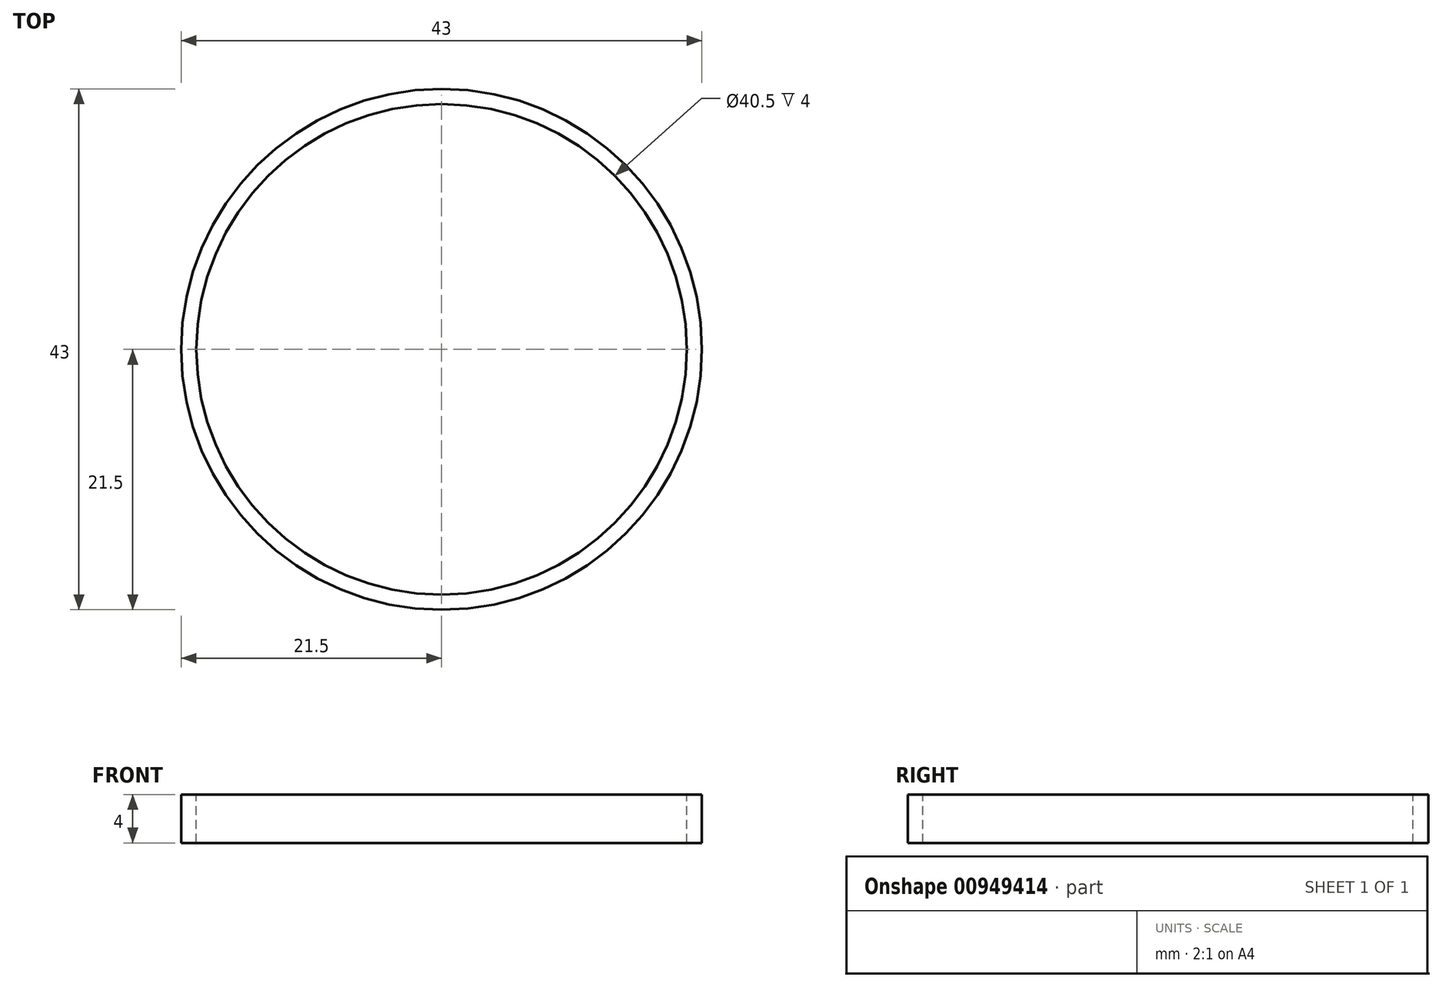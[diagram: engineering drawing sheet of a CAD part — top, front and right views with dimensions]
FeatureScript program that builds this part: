
annotation { "Feature Type Name" : "Feature", "Feature Type Description" : "" }
export const myFeature = defineFeature(function(context is Context, id is Id, definition is map)
    precondition{}
    {
        {
            var Q0;
            Q0=qCreatedBy(makeId("Top.planeOp"),FACE);
            var sketch = newSketch(context, id + "F0", { "sketchPlane" : qUnion([Q0])});
            skCircle(sketch, "E0", {"center": v(0, 0) * mm, "radius": 21.5 * mm});
            skCircle(sketch, "E1", {"center": v(0, 0) * mm, "radius": 20.25 * mm});
            skSolve(sketch);
        }
        {
            var Q0;
            Q0=makeQuery(id+"F0.imprint","IMPRINT",FACE,{"disambiguationData":[TD([[makeQuery(id+"F0.imprint","IMPRINT",EDGE,{"derivedFrom":sQuery(id+"F0.wireOp",EDGE,"E0")}),1.0]])]});
            extrude(context, id + "F1", {"entities" : qUnion([Q0]), "oppositeDirection" : true, "depth" : 4 * mm, "offsetDistance" : 25 * mm});
        }
    });
